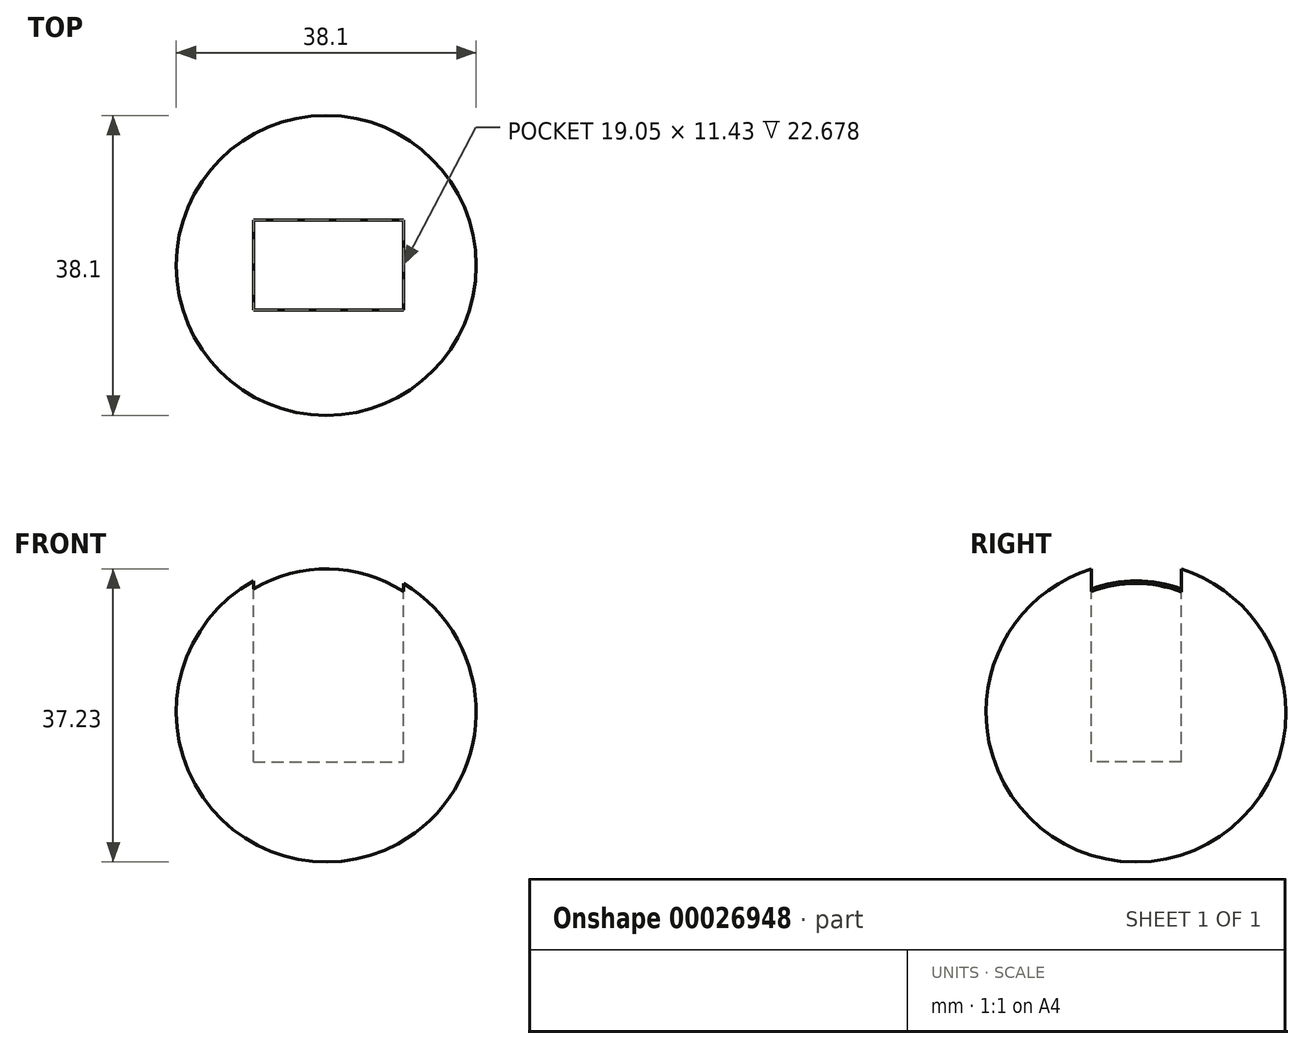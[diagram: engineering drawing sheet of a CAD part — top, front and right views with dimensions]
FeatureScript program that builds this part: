
annotation { "Feature Type Name" : "Feature", "Feature Type Description" : "" }
export const myFeature = defineFeature(function(context is Context, id is Id, definition is map)
    precondition{}
    {
        {
            var Q0;
            Q0=qCreatedBy(makeId("Top.planeOp"),FACE);
            var sketch = newSketch(context, id + "F0", { "sketchPlane" : qUnion([Q0])});
            skLineSegment(sketch, "E0", {"start": v(0, 24.74) * mm, "end": v(0, -13.36) * mm});
            skArc(sketch, "E1", {"start": v(0, -13.36) * mm, "mid": v(19.05, 5.69) * mm, "end": v(0, 24.74) * mm});
            skSolve(sketch);
        }
        {
            var Q0;
            Q0 = qSketchRegion(id + "F0", true);
            var Q1;
            Q1=sQuery(id+"F0.wireOp",EDGE,"E0");
            revolve(context, id + "F1", {"entities" : qUnion([Q0]), "axis" : qUnion([Q1]), "revolveType" : RevolveType.FULL});
        }
        {
            var Q0;
            Q0=qCreatedBy(makeId("Top.planeOp"),FACE);
            cPlane(context, id + "F2", {"entities" : qUnion([Q0]), "cplaneType" : CPlaneType.OFFSET, "offset" : 19.05 * mm, "width" : 152.4 * mm, "height" : 152.4 * mm});
        }
        {
            var Q0;
            Q0=qCreatedBy(id+"F2.planeOp",FACE);
            var sketch = newSketch(context, id + "F3", { "sketchPlane" : qUnion([Q0])});
            skLineSegment(sketch, "E2.bottom", {"start": v(-9.24, 11.43) * mm, "end": v(9.81, 11.43) * mm});
            skLineSegment(sketch, "E2.top", {"start": v(-9.24, 0) * mm, "end": v(9.81, 0) * mm});
            skLineSegment(sketch, "E2.left", {"start": v(-9.24, 11.43) * mm, "end": v(-9.24, 0) * mm});
            skLineSegment(sketch, "E2.right", {"start": v(9.81, 11.43) * mm, "end": v(9.81, 0) * mm});
            skSolve(sketch);
        }
        {
            var Q0;
            Q0 = qSketchRegion(id + "F3", true);
            extrude(context, id + "F4", {"entities" : qUnion([Q0]), "operationType" : NewBodyOperationType.REMOVE, "oppositeDirection" : true, "depth" : 25.4 * mm});
        }
    });
